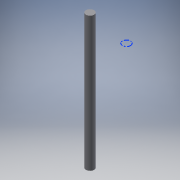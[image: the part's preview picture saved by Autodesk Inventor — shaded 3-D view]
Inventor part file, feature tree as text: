
AUTODESK INVENTOR PART (.ipt)
format: ipt  version: 2018 (Build 220112000, 112)  size: 90,624 bytes
history: native  units: mm
features: sketch x1, plane x1, extrude x1
ambient origin geometry x8: Origin, YZ Plane, XZ Plane, XY Plane, X Axis, Y Axis, Z Axis, Center Point
bodies: Solid1 (feature_tree)
feature tree (3):
  sketch  "Sketch1"  dims[d0=4.6mm d1=10.0mm d2=0.0mm]
  plane  "Work Plane1"
  extrude  "Extrusion1"  Depth=10.0mm TaperAngle=0.0deg
